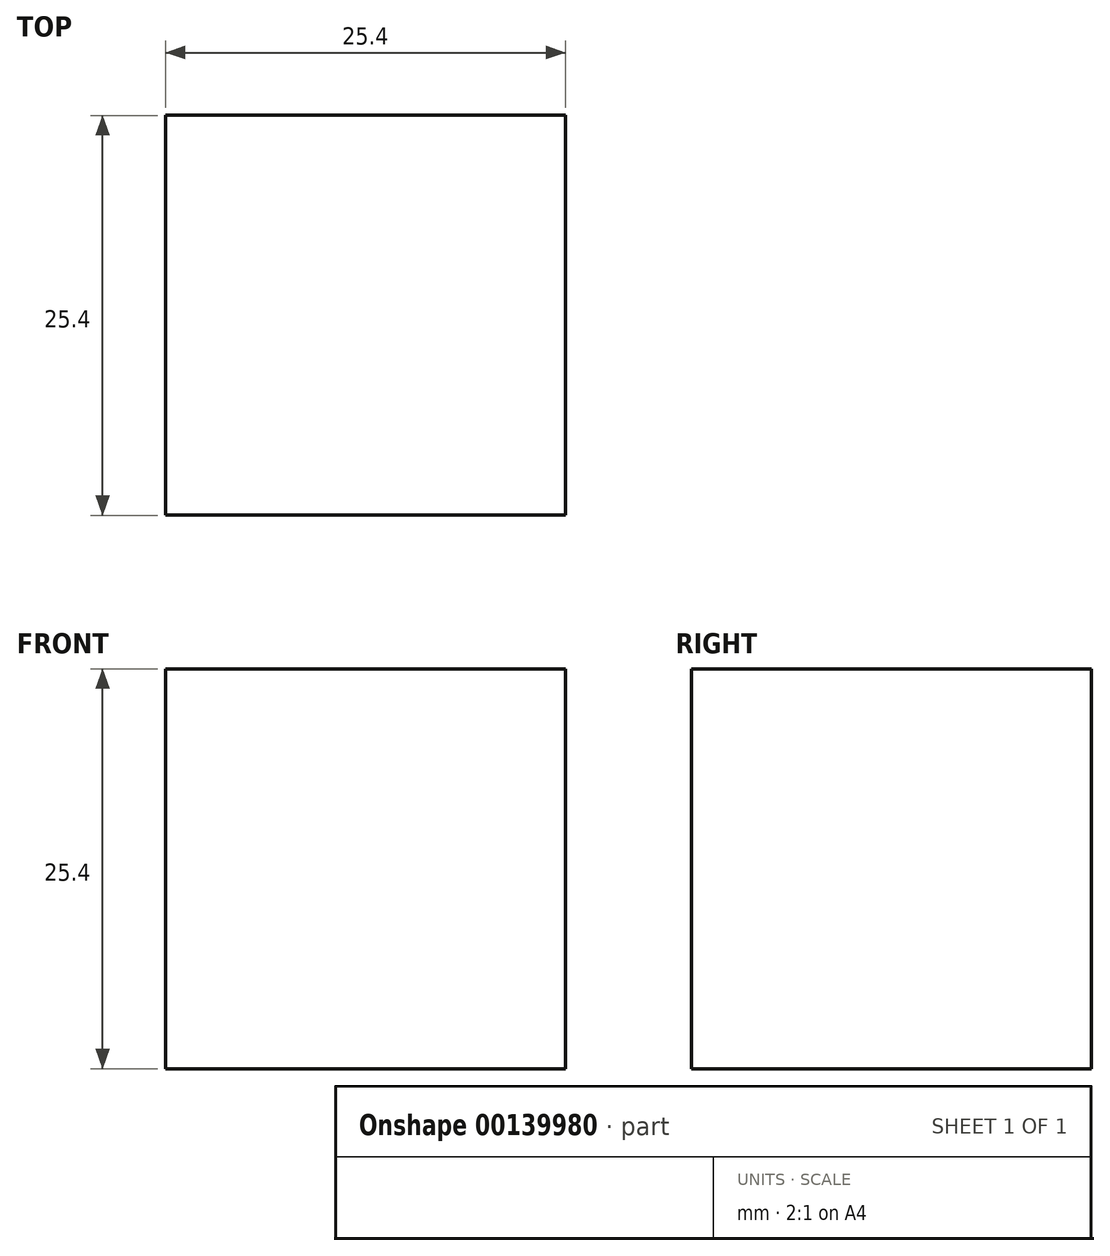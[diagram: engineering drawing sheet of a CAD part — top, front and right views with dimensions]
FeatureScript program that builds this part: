
annotation { "Feature Type Name" : "Feature", "Feature Type Description" : "" }
export const myFeature = defineFeature(function(context is Context, id is Id, definition is map)
    precondition{}
    {
        {
            var Q0;
            Q0=qCreatedBy(makeId("Top.planeOp"),FACE);
            var sketch = newSketch(context, id + "F0", { "sketchPlane" : qUnion([Q0])});
            skLineSegment(sketch, "E0.bottom", {"start": v(12.7, 8.48) * mm, "end": v(-12.7, 8.48) * mm});
            skLineSegment(sketch, "E0.top", {"start": v(12.7, -16.92) * mm, "end": v(-12.7, -16.92) * mm});
            skLineSegment(sketch, "E0.left", {"start": v(12.7, 8.48) * mm, "end": v(12.7, -16.92) * mm});
            skLineSegment(sketch, "E0.right", {"start": v(-12.7, 8.48) * mm, "end": v(-12.7, -16.92) * mm});
            skPoint(sketch, "E0.middle", {"position": v(0, -4.22) * mm});
            skSolve(sketch);
        }
        {
            var Q0;
            Q0 = qSketchRegion(id + "F0", true);
            extrude(context, id + "F1", {"entities" : qUnion([Q0]), "depth" : 25.4 * mm});
        }
    });
